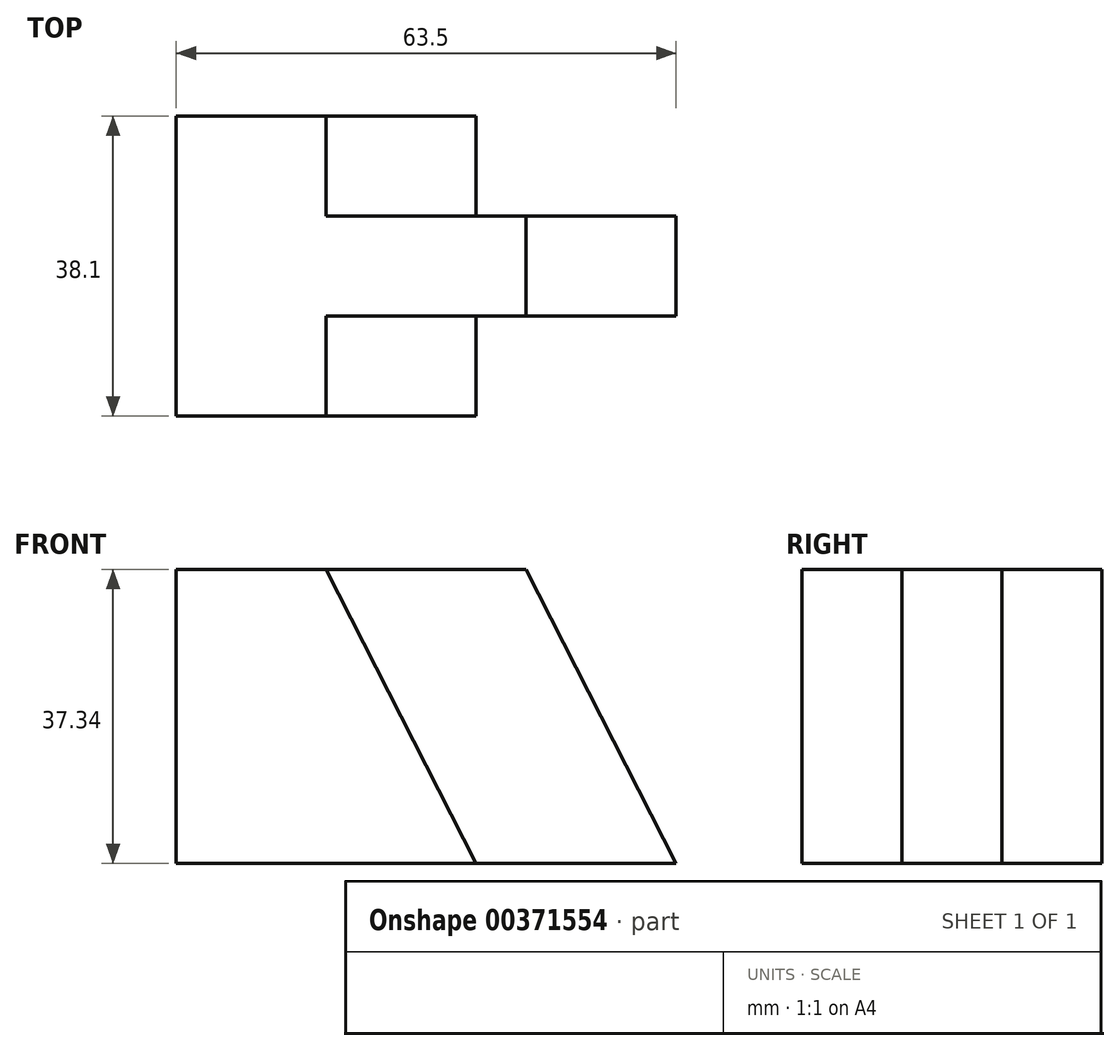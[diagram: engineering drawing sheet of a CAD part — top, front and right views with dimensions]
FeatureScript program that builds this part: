
annotation { "Feature Type Name" : "Feature", "Feature Type Description" : "" }
export const myFeature = defineFeature(function(context is Context, id is Id, definition is map)
    precondition{}
    {
        {
            var Q0;
            Q0=qCreatedBy(makeId("Front.planeOp"),FACE);
            var sketch = newSketch(context, id + "F0", { "sketchPlane" : qUnion([Q0])});
            skLineSegment(sketch, "E0", {"start": v(0, 0) * mm, "end": v(63.5, 0) * mm});
            skLineSegment(sketch, "E1", {"start": v(63.5, 0) * mm, "end": v(44.45, 37.34) * mm});
            skLineSegment(sketch, "E2", {"start": v(44.45, 37.34) * mm, "end": v(0, 37.34) * mm});
            skLineSegment(sketch, "E3", {"start": v(0, 37.34) * mm, "end": v(0, 0) * mm});
            skSolve(sketch);
        }
        {
            var Q0;
            Q0 = qSketchRegion(id + "F0", true);
            extrude(context, id + "F1", {"entities" : qUnion([Q0]), "depth" : 38.1 * mm});
        }
        {
            var Q0;
            Q0=makeQuery(id+"F1.opExtrude","CAP_FACE",FACE,{"disambiguationData":[OSD([sQuery(id+"F0.wireOp",EDGE,"E0"),sQuery(id+"F0.wireOp",EDGE,"E1"),sQuery(id+"F0.wireOp",EDGE,"E2"),sQuery(id+"F0.wireOp",EDGE,"E3")])],"isStart":false});
            var sketch = newSketch(context, id + "F2", { "sketchPlane" : qUnion([Q0])});
            skLineSegment(sketch, "E4", {"start": v(19.05, 37.34) * mm, "end": v(38.1, 0) * mm});
            skSolve(sketch);
        }
        {
            var Q0;
            Q0 = qSketchRegion(id + "F2", true);
            var Q1;
            {var subQ0=sQuery(id+"F2.wireOp",EDGE,"E4");Q1=makeQuery(id+"F2.imprint","IMPRINT",FACE,{"disambiguationData":[TD([[makeQuery(id+"F2.imprint","IMPRINT",EDGE,{"derivedFrom":subQ0}),1.0]])]});}
            extrude(context, id + "F3", {"entities" : qUnion([Q0, Q1]), "operationType" : NewBodyOperationType.REMOVE, "oppositeDirection" : true, "depth" : 12.7 * mm});
        }
        {
            var Q0;
            Q0=makeQuery(id+"F1.opExtrude","CAP_FACE",FACE,{"disambiguationData":[OSD([sQuery(id+"F0.wireOp",EDGE,"E0"),sQuery(id+"F0.wireOp",EDGE,"E1"),sQuery(id+"F0.wireOp",EDGE,"E2"),sQuery(id+"F0.wireOp",EDGE,"E3")])],"isStart":true});
            var sketch = newSketch(context, id + "F4", { "sketchPlane" : qUnion([Q0])});
            skLineSegment(sketch, "E5", {"start": v(-19.05, 37.34) * mm, "end": v(-38.1, 0) * mm});
            skSolve(sketch);
        }
        {
            var Q0;
            Q0 = qSketchRegion(id + "F4", true);
            var Q1;
            {var subQ0=sQuery(id+"F4.wireOp",EDGE,"E5");Q1=makeQuery(id+"F4.imprint","IMPRINT",FACE,{"disambiguationData":[TD([[makeQuery(id+"F4.imprint","IMPRINT",EDGE,{"derivedFrom":subQ0}),-1.0]])]});}
            extrude(context, id + "F5", {"entities" : qUnion([Q0, Q1]), "operationType" : NewBodyOperationType.REMOVE, "oppositeDirection" : true, "depth" : 12.7 * mm});
        }
    });
